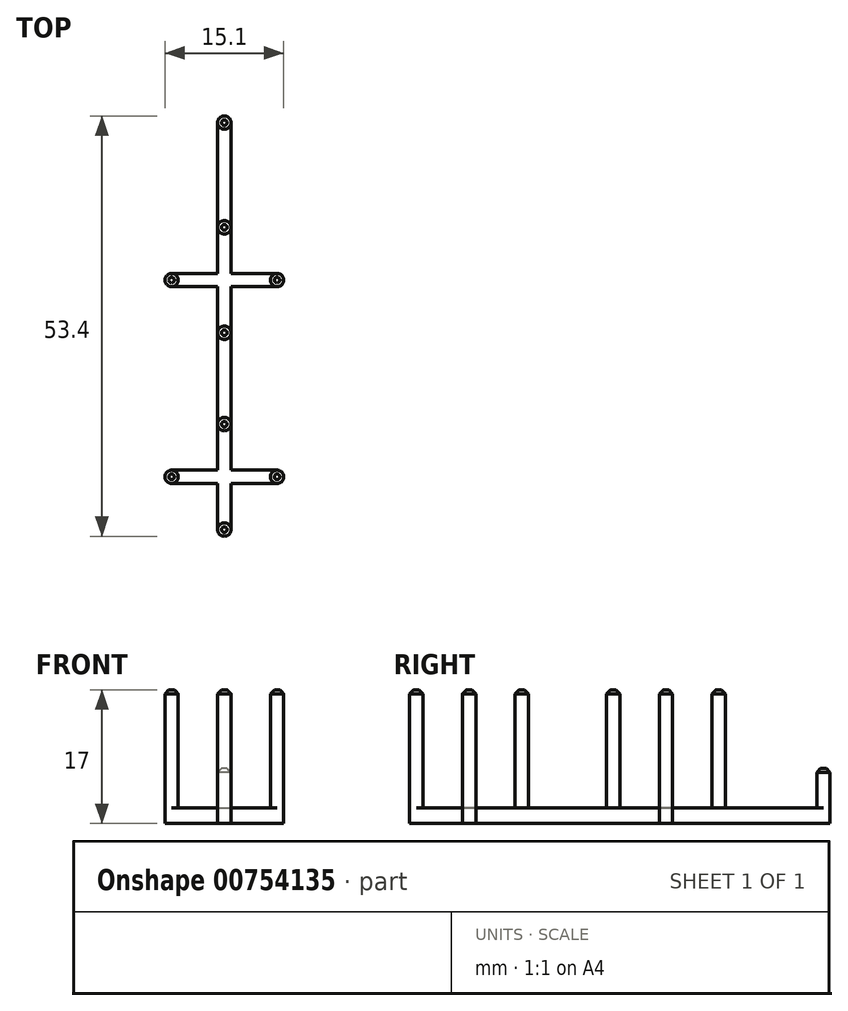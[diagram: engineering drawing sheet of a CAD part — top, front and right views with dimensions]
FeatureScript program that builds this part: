
annotation { "Feature Type Name" : "Feature", "Feature Type Description" : "" }
export const myFeature = defineFeature(function(context is Context, id is Id, definition is map)
    precondition{}
    {
        {
            var Q0;
            Q0=qCreatedBy(makeId("Top.planeOp"),FACE);
            var sketch = newSketch(context, id + "F0", { "sketchPlane" : qUnion([Q0])});
            skLineSegment(sketch, "E0", {"start": v(-6.7, 0) * mm, "end": v(6.7, 0) * mm});
            skLineSegment(sketch, "E1", {"start": v(0, -6.7) * mm, "end": v(0, 6.7) * mm});
            skCircle(sketch, "E2", {"center": v(-6.7, 0) * mm, "radius": 0.85 * mm});
            skCircle(sketch, "E3", {"center": v(0, -6.7) * mm, "radius": 0.85 * mm});
            skCircle(sketch, "E4", {"center": v(6.7, 0) * mm, "radius": 0.85 * mm});
            skCircle(sketch, "E5", {"center": v(0, 6.7) * mm, "radius": 0.85 * mm});
            skLineSegment(sketch, "E6.top", {"start": v(-0.85, 45) * mm, "end": v(0.85, 45) * mm});
            skCircle(sketch, "E7", {"center": v(0, 18.3) * mm, "radius": 0.85 * mm});
            skCircle(sketch, "E8", {"center": v(0, 31.7) * mm, "radius": 0.85 * mm});
            skLineSegment(sketch, "E9", {"start": v(0, 18.3) * mm, "end": v(0, 31.7) * mm});
            skPoint(sketch, "E10", {"position": v(0, 25) * mm});
            skLineSegment(sketch, "E11", {"start": v(-6.7, 25) * mm, "end": v(6.7, 25) * mm});
            skCircle(sketch, "E12", {"center": v(-6.7, 25) * mm, "radius": 0.85 * mm});
            skCircle(sketch, "E13", {"center": v(6.7, 25) * mm, "radius": 0.85 * mm});
            skLineSegment(sketch, "E14.bottom", {"start": v(-7.55, 24.15) * mm, "end": v(7.55, 24.15) * mm});
            skLineSegment(sketch, "E14.top", {"start": v(-7.55, 25.85) * mm, "end": v(7.55, 25.85) * mm});
            skLineSegment(sketch, "E14.left", {"start": v(-7.55, 24.15) * mm, "end": v(-7.55, 25.85) * mm});
            skLineSegment(sketch, "E14.right", {"start": v(7.55, 24.15) * mm, "end": v(7.55, 25.85) * mm});
            skCircle(sketch, "E15", {"center": v(0, 45) * mm, "radius": 0.85 * mm});
            skLineSegment(sketch, "E16", {"start": v(-6.7, -0.85) * mm, "end": v(6.7, -0.85) * mm});
            skLineSegment(sketch, "E17", {"start": v(-6.7, 0.85) * mm, "end": v(6.7, 0.85) * mm});
            skLineSegment(sketch, "E18", {"start": v(0.85, -6.7) * mm, "end": v(0.85, 45) * mm});
            skLineSegment(sketch, "E19", {"start": v(-0.85, -6.7) * mm, "end": v(-0.85, 45) * mm});
            skSolve(sketch);
        }
        {
            var Q0;
            {var subQ5=sQuery(id+"F0.wireOp",EDGE,"E6.top");Q0=makeQuery(id+"F0.imprint","IMPRINT",FACE,{"disambiguationData":[TD([[makeQuery(id+"F0.imprint","IMPRINT",EDGE,{"derivedFrom":subQ5}),-1.0]])]});}
            var Q1;
            {var subQ0=sQuery(id+"F0.wireOp",EDGE,"E5");var subQ1=makeQuery(id+"F0.imprint","INTERSECT",VERTEX,{"derivedFrom":[subQ0,sQuery(id+"F0.wireOp",EDGE,"E6.left")]});Q1=makeQuery(id+"F0.imprint","IMPRINT",FACE,{"disambiguationData":[TD([[makeQuery(id+"F0.imprint","IMPRINT",EDGE,{"disambiguationData":[TD([[subQ1,1.0]])],"derivedFrom":subQ0}),1.0]])]});}
            var Q2;
            {var subQ0=sQuery(id+"F0.wireOp",EDGE,"E5");var subQ1=sQuery(id+"F0.wireOp",EDGE,"E1");var subQ2=makeQuery(id+"F0.imprint","INTERSECT",VERTEX,{"derivedFrom":[subQ1,subQ0]});Q2=makeQuery(id+"F0.imprint","IMPRINT",FACE,{"disambiguationData":[TD([[makeQuery(id+"F0.imprint","IMPRINT",EDGE,{"disambiguationData":[TD([[subQ2,1.0]])],"derivedFrom":subQ1}),-1.0]])]});}
            var Q3;
            {var subQ0=sQuery(id+"F0.wireOp",EDGE,"E5");var subQ1=sQuery(id+"F0.wireOp",EDGE,"E1");var subQ2=makeQuery(id+"F0.imprint","INTERSECT",VERTEX,{"derivedFrom":[subQ1,subQ0]});Q3=makeQuery(id+"F0.imprint","IMPRINT",FACE,{"disambiguationData":[TD([[makeQuery(id+"F0.imprint","IMPRINT",EDGE,{"disambiguationData":[TD([[subQ2,1.0]])],"derivedFrom":subQ1}),1.0]])]});}
            var Q4;
            {var subQ0=sQuery(id+"F0.wireOp",EDGE,"E6.left");var subQ1=sQuery(id+"F0.wireOp",EDGE,"E0");var subQ2=makeQuery(id+"F0.imprint","INTERSECT",VERTEX,{"derivedFrom":[subQ1,subQ0]});Q4=makeQuery(id+"F0.imprint","IMPRINT",FACE,{"disambiguationData":[TD([[makeQuery(id+"F0.imprint","IMPRINT",EDGE,{"disambiguationData":[TD([[subQ2,-1.0]])],"derivedFrom":subQ1}),1.0]])]});}
            var Q5;
            {var subQ0=sQuery(id+"F0.wireOp",EDGE,"E2");var subQ1=sQuery(id+"F0.wireOp",EDGE,"E0");var subQ2=makeQuery(id+"F0.imprint","INTERSECT",VERTEX,{"derivedFrom":[subQ1,subQ0]});Q5=makeQuery(id+"F0.imprint","IMPRINT",FACE,{"disambiguationData":[TD([[makeQuery(id+"F0.imprint","IMPRINT",EDGE,{"disambiguationData":[TD([[subQ2,-1.0]])],"derivedFrom":subQ1}),-1.0]])]});}
            var Q6;
            {var subQ0=sQuery(id+"F0.wireOp",EDGE,"E2");var subQ1=makeQuery(id+"F0.imprint","INTERSECT",VERTEX,{"derivedFrom":[sQuery(id+"F0.wireOp",EDGE,"E0"),subQ0]});Q6=makeQuery(id+"F0.imprint","IMPRINT",FACE,{"disambiguationData":[TD([[makeQuery(id+"F0.imprint","IMPRINT",EDGE,{"disambiguationData":[TD([[subQ1,-1.0]])],"derivedFrom":subQ0}),1.0]])]});}
            var Q7;
            {var subQ0=sQuery(id+"F0.wireOp",EDGE,"E1");var subQ1=sQuery(id+"F0.wireOp",EDGE,"E0");var subQ2=makeQuery(id+"F0.imprint","INTERSECT",VERTEX,{"derivedFrom":[subQ1,subQ0]});Q7=makeQuery(id+"F0.imprint","IMPRINT",FACE,{"disambiguationData":[TD([[makeQuery(id+"F0.imprint","IMPRINT",EDGE,{"disambiguationData":[TD([[subQ2,-1.0]])],"derivedFrom":subQ1}),1.0]])]});}
            var Q8;
            {var subQ0=sQuery(id+"F0.wireOp",EDGE,"E1");var subQ1=sQuery(id+"F0.wireOp",EDGE,"E0");var subQ2=makeQuery(id+"F0.imprint","INTERSECT",VERTEX,{"derivedFrom":[subQ1,subQ0]});Q8=makeQuery(id+"F0.imprint","IMPRINT",FACE,{"disambiguationData":[TD([[makeQuery(id+"F0.imprint","IMPRINT",EDGE,{"disambiguationData":[TD([[subQ2,-1.0]])],"derivedFrom":subQ1}),-1.0]])]});}
            var Q9;
            {var subQ0=sQuery(id+"F0.wireOp",EDGE,"E6.left");var subQ1=sQuery(id+"F0.wireOp",EDGE,"E0");var subQ2=makeQuery(id+"F0.imprint","INTERSECT",VERTEX,{"derivedFrom":[subQ1,subQ0]});Q9=makeQuery(id+"F0.imprint","IMPRINT",FACE,{"disambiguationData":[TD([[makeQuery(id+"F0.imprint","IMPRINT",EDGE,{"disambiguationData":[TD([[subQ2,-1.0]])],"derivedFrom":subQ1}),-1.0]])]});}
            var Q10;
            {var subQ0=sQuery(id+"F0.wireOp",EDGE,"E2");var subQ1=sQuery(id+"F0.wireOp",EDGE,"E0");var subQ2=makeQuery(id+"F0.imprint","INTERSECT",VERTEX,{"derivedFrom":[subQ1,subQ0]});Q10=makeQuery(id+"F0.imprint","IMPRINT",FACE,{"disambiguationData":[TD([[makeQuery(id+"F0.imprint","IMPRINT",EDGE,{"disambiguationData":[TD([[subQ2,-1.0]])],"derivedFrom":subQ1}),1.0]])]});}
            var Q11;
            {var subQ0=sQuery(id+"F0.wireOp",EDGE,"E4");var subQ1=sQuery(id+"F0.wireOp",EDGE,"E0");var subQ2=makeQuery(id+"F0.imprint","INTERSECT",VERTEX,{"derivedFrom":[subQ1,subQ0]});Q11=makeQuery(id+"F0.imprint","IMPRINT",FACE,{"disambiguationData":[TD([[makeQuery(id+"F0.imprint","IMPRINT",EDGE,{"disambiguationData":[TD([[subQ2,1.0]])],"derivedFrom":subQ1}),1.0]])]});}
            var Q12;
            {var subQ0=sQuery(id+"F0.wireOp",EDGE,"E4");var subQ1=makeQuery(id+"F0.imprint","INTERSECT",VERTEX,{"derivedFrom":[subQ0,sQuery(id+"F0.wireOp",EDGE,"UeLpGbLd-B8RJ-5YED-L5t8-W8zW61iBtvWg.bottom")]});Q12=makeQuery(id+"F0.imprint","IMPRINT",FACE,{"disambiguationData":[TD([[makeQuery(id+"F0.imprint","IMPRINT",EDGE,{"disambiguationData":[TD([[subQ1,1.0]])],"derivedFrom":subQ0}),1.0]])]});}
            var Q13;
            {var subQ0=sQuery(id+"F0.wireOp",EDGE,"E4");var subQ1=sQuery(id+"F0.wireOp",EDGE,"E0");var subQ2=makeQuery(id+"F0.imprint","INTERSECT",VERTEX,{"derivedFrom":[subQ1,subQ0]});Q13=makeQuery(id+"F0.imprint","IMPRINT",FACE,{"disambiguationData":[TD([[makeQuery(id+"F0.imprint","IMPRINT",EDGE,{"disambiguationData":[TD([[subQ2,1.0]])],"derivedFrom":subQ1}),-1.0]])]});}
            var Q14;
            {var subQ0=sQuery(id+"F0.wireOp",EDGE,"E3");var subQ1=sQuery(id+"F0.wireOp",EDGE,"E1");var subQ2=makeQuery(id+"F0.imprint","INTERSECT",VERTEX,{"derivedFrom":[subQ1,subQ0]});Q14=makeQuery(id+"F0.imprint","IMPRINT",FACE,{"disambiguationData":[TD([[makeQuery(id+"F0.imprint","IMPRINT",EDGE,{"disambiguationData":[TD([[subQ2,-1.0]])],"derivedFrom":subQ1}),-1.0]])]});}
            var Q15;
            {var subQ0=sQuery(id+"F0.wireOp",EDGE,"E3");var subQ1=sQuery(id+"F0.wireOp",EDGE,"E1");var subQ2=makeQuery(id+"F0.imprint","INTERSECT",VERTEX,{"derivedFrom":[subQ1,subQ0]});Q15=makeQuery(id+"F0.imprint","IMPRINT",FACE,{"disambiguationData":[TD([[makeQuery(id+"F0.imprint","IMPRINT",EDGE,{"disambiguationData":[TD([[subQ2,-1.0]])],"derivedFrom":subQ1}),1.0]])]});}
            var Q16;
            {var subQ0=sQuery(id+"F0.wireOp",EDGE,"E3");var subQ1=makeQuery(id+"F0.imprint","INTERSECT",VERTEX,{"derivedFrom":[sQuery(id+"F0.wireOp",EDGE,"E1"),subQ0]});Q16=makeQuery(id+"F0.imprint","IMPRINT",FACE,{"disambiguationData":[TD([[makeQuery(id+"F0.imprint","IMPRINT",EDGE,{"disambiguationData":[TD([[subQ1,1.0]])],"derivedFrom":subQ0}),1.0]])]});}
            var Q17;
            {var subQ0=sQuery(id+"F0.wireOp",EDGE,"E6.left");var subQ1=sQuery(id+"F0.wireOp",EDGE,"E5");var subQ2=makeQuery(id+"F0.imprint","INTERSECT",VERTEX,{"derivedFrom":[subQ1,subQ0]});Q17=makeQuery(id+"F0.imprint","IMPRINT",FACE,{"disambiguationData":[TD([[makeQuery(id+"F0.imprint","IMPRINT",EDGE,{"disambiguationData":[TD([[subQ2,1.0]])],"derivedFrom":subQ1}),-1.0]])]});}
            var Q18;
            {var subQ0=sQuery(id+"F0.wireOp",EDGE,"E7");var subQ1=makeQuery(id+"F0.imprint","INTERSECT",VERTEX,{"derivedFrom":[sQuery(id+"F0.wireOp",EDGE,"E6.right"),subQ0]});Q18=makeQuery(id+"F0.imprint","IMPRINT",FACE,{"disambiguationData":[TD([[makeQuery(id+"F0.imprint","IMPRINT",EDGE,{"disambiguationData":[TD([[subQ1,-1.0]])],"derivedFrom":subQ0}),1.0]])]});}
            var Q19;
            {var subQ0=sQuery(id+"F0.wireOp",EDGE,"E7");var subQ1=sQuery(id+"F0.wireOp",EDGE,"E6.right");var subQ2=makeQuery(id+"F0.imprint","INTERSECT",VERTEX,{"derivedFrom":[subQ1,subQ0]});Q19=makeQuery(id+"F0.imprint","IMPRINT",FACE,{"disambiguationData":[TD([[makeQuery(id+"F0.imprint","IMPRINT",EDGE,{"disambiguationData":[TD([[subQ2,-1.0]])],"derivedFrom":subQ1}),1.0]])]});}
            var Q20;
            {var subQ0=sQuery(id+"F0.wireOp",EDGE,"E14.bottom");var subQ1=sQuery(id+"F0.wireOp",EDGE,"E6.right");var subQ2=makeQuery(id+"F0.imprint","INTERSECT",VERTEX,{"derivedFrom":[subQ1,subQ0]});Q20=makeQuery(id+"F0.imprint","IMPRINT",FACE,{"disambiguationData":[TD([[makeQuery(id+"F0.imprint","IMPRINT",EDGE,{"disambiguationData":[TD([[subQ2,-1.0]])],"derivedFrom":subQ1}),1.0]])]});}
            var Q21;
            {var subQ0=sQuery(id+"F0.wireOp",EDGE,"E14.top");var subQ1=sQuery(id+"F0.wireOp",EDGE,"E6.right");var subQ2=makeQuery(id+"F0.imprint","INTERSECT",VERTEX,{"derivedFrom":[subQ1,subQ0]});Q21=makeQuery(id+"F0.imprint","IMPRINT",FACE,{"disambiguationData":[TD([[makeQuery(id+"F0.imprint","IMPRINT",EDGE,{"disambiguationData":[TD([[subQ2,1.0]])],"derivedFrom":subQ1}),1.0]])]});}
            var Q22;
            {var subQ0=sQuery(id+"F0.wireOp",EDGE,"E14.top");var subQ1=sQuery(id+"F0.wireOp",EDGE,"E6.right");var subQ2=makeQuery(id+"F0.imprint","INTERSECT",VERTEX,{"derivedFrom":[subQ1,subQ0]});Q22=makeQuery(id+"F0.imprint","IMPRINT",FACE,{"disambiguationData":[TD([[makeQuery(id+"F0.imprint","IMPRINT",EDGE,{"disambiguationData":[TD([[subQ2,-1.0]])],"derivedFrom":subQ1}),1.0]])]});}
            var Q23;
            {var subQ0=sQuery(id+"F0.wireOp",EDGE,"E14.top");var subQ1=sQuery(id+"F0.wireOp",EDGE,"E6.right");var subQ2=makeQuery(id+"F0.imprint","INTERSECT",VERTEX,{"derivedFrom":[subQ1,subQ0]});Q23=makeQuery(id+"F0.imprint","IMPRINT",FACE,{"disambiguationData":[TD([[makeQuery(id+"F0.imprint","IMPRINT",EDGE,{"disambiguationData":[TD([[subQ2,1.0]])],"derivedFrom":subQ1}),-1.0]])]});}
            var Q24;
            {var subQ0=sQuery(id+"F0.wireOp",EDGE,"E14.bottom");var subQ1=sQuery(id+"F0.wireOp",EDGE,"E6.right");var subQ2=makeQuery(id+"F0.imprint","INTERSECT",VERTEX,{"derivedFrom":[subQ1,subQ0]});Q24=makeQuery(id+"F0.imprint","IMPRINT",FACE,{"disambiguationData":[TD([[makeQuery(id+"F0.imprint","IMPRINT",EDGE,{"disambiguationData":[TD([[subQ2,-1.0]])],"derivedFrom":subQ1}),-1.0]])]});}
            var Q25;
            {var subQ0=sQuery(id+"F0.wireOp",EDGE,"E13");var subQ1=makeQuery(id+"F0.imprint","INTERSECT",VERTEX,{"derivedFrom":[subQ0,sQuery(id+"F0.wireOp",EDGE,"E14.top")]});Q25=makeQuery(id+"F0.imprint","IMPRINT",FACE,{"disambiguationData":[TD([[makeQuery(id+"F0.imprint","IMPRINT",EDGE,{"disambiguationData":[TD([[subQ1,1.0]])],"derivedFrom":subQ0}),1.0]])]});}
            var Q26;
            {var subQ0=sQuery(id+"F0.wireOp",EDGE,"E7");var subQ1=sQuery(id+"F0.wireOp",EDGE,"E6.left");var subQ2=makeQuery(id+"F0.imprint","INTERSECT",VERTEX,{"derivedFrom":[subQ1,subQ0]});Q26=makeQuery(id+"F0.imprint","IMPRINT",FACE,{"disambiguationData":[TD([[makeQuery(id+"F0.imprint","IMPRINT",EDGE,{"disambiguationData":[TD([[subQ2,-1.0]])],"derivedFrom":subQ1}),-1.0]])]});}
            var Q27;
            {var subQ0=sQuery(id+"F0.wireOp",EDGE,"E14.bottom");var subQ1=sQuery(id+"F0.wireOp",EDGE,"E6.left");var subQ2=makeQuery(id+"F0.imprint","INTERSECT",VERTEX,{"derivedFrom":[subQ1,subQ0]});Q27=makeQuery(id+"F0.imprint","IMPRINT",FACE,{"disambiguationData":[TD([[makeQuery(id+"F0.imprint","IMPRINT",EDGE,{"disambiguationData":[TD([[subQ2,-1.0]])],"derivedFrom":subQ1}),-1.0]])]});}
            var Q28;
            {var subQ0=sQuery(id+"F0.wireOp",EDGE,"E14.top");var subQ1=sQuery(id+"F0.wireOp",EDGE,"E6.left");var subQ2=makeQuery(id+"F0.imprint","INTERSECT",VERTEX,{"derivedFrom":[subQ1,subQ0]});Q28=makeQuery(id+"F0.imprint","IMPRINT",FACE,{"disambiguationData":[TD([[makeQuery(id+"F0.imprint","IMPRINT",EDGE,{"disambiguationData":[TD([[subQ2,1.0]])],"derivedFrom":subQ1}),-1.0]])]});}
            var Q29;
            {var subQ0=sQuery(id+"F0.wireOp",EDGE,"E14.top");var subQ1=sQuery(id+"F0.wireOp",EDGE,"E6.left");var subQ2=makeQuery(id+"F0.imprint","INTERSECT",VERTEX,{"derivedFrom":[subQ1,subQ0]});Q29=makeQuery(id+"F0.imprint","IMPRINT",FACE,{"disambiguationData":[TD([[makeQuery(id+"F0.imprint","IMPRINT",EDGE,{"disambiguationData":[TD([[subQ2,1.0]])],"derivedFrom":subQ1}),1.0]])]});}
            var Q30;
            {var subQ0=sQuery(id+"F0.wireOp",EDGE,"E14.bottom");var subQ1=sQuery(id+"F0.wireOp",EDGE,"E6.left");var subQ2=makeQuery(id+"F0.imprint","INTERSECT",VERTEX,{"derivedFrom":[subQ1,subQ0]});Q30=makeQuery(id+"F0.imprint","IMPRINT",FACE,{"disambiguationData":[TD([[makeQuery(id+"F0.imprint","IMPRINT",EDGE,{"disambiguationData":[TD([[subQ2,-1.0]])],"derivedFrom":subQ1}),1.0]])]});}
            var Q31;
            {var subQ0=sQuery(id+"F0.wireOp",EDGE,"E12");var subQ1=makeQuery(id+"F0.imprint","INTERSECT",VERTEX,{"derivedFrom":[sQuery(id+"F0.wireOp",EDGE,"E11"),subQ0]});Q31=makeQuery(id+"F0.imprint","IMPRINT",FACE,{"disambiguationData":[TD([[makeQuery(id+"F0.imprint","IMPRINT",EDGE,{"disambiguationData":[TD([[subQ1,-1.0]])],"derivedFrom":subQ0}),1.0]])]});}
            var Q32;
            {var subQ0=sQuery(id+"F0.wireOp",EDGE,"E14.top");var subQ1=sQuery(id+"F0.wireOp",EDGE,"E6.left");var subQ2=makeQuery(id+"F0.imprint","INTERSECT",VERTEX,{"derivedFrom":[subQ1,subQ0]});Q32=makeQuery(id+"F0.imprint","IMPRINT",FACE,{"disambiguationData":[TD([[makeQuery(id+"F0.imprint","IMPRINT",EDGE,{"disambiguationData":[TD([[subQ2,-1.0]])],"derivedFrom":subQ1}),-1.0]])]});}
            var Q33;
            {var subQ0=sQuery(id+"F0.wireOp",EDGE,"E8");var subQ1=makeQuery(id+"F0.imprint","INTERSECT",VERTEX,{"derivedFrom":[sQuery(id+"F0.wireOp",EDGE,"E6.left"),subQ0]});Q33=makeQuery(id+"F0.imprint","IMPRINT",FACE,{"disambiguationData":[TD([[makeQuery(id+"F0.imprint","IMPRINT",EDGE,{"disambiguationData":[TD([[subQ1,1.0]])],"derivedFrom":subQ0}),1.0]])]});}
            var Q34;
            {var subQ1=sQuery(id+"F0.wireOp",EDGE,"E6.left");var subQ4=sQuery(id+"F0.wireOp",EDGE,"E8");var subQ5=makeQuery(id+"F0.imprint","INTERSECT",VERTEX,{"derivedFrom":[subQ1,subQ4]});Q34=makeQuery(id+"F0.imprint","IMPRINT",FACE,{"disambiguationData":[TD([[makeQuery(id+"F0.imprint","IMPRINT",EDGE,{"disambiguationData":[TD([[subQ5,1.0]])],"derivedFrom":subQ4}),-1.0]])]});}
            var Q35;
            {var subQ0=sQuery(id+"F0.wireOp",EDGE,"E9");var subQ1=sQuery(id+"F0.wireOp",EDGE,"E7");var subQ2=makeQuery(id+"F0.imprint","INTERSECT",VERTEX,{"derivedFrom":[subQ1,subQ0]});Q35=makeQuery(id+"F0.imprint","IMPRINT",FACE,{"disambiguationData":[TD([[makeQuery(id+"F0.imprint","IMPRINT",EDGE,{"disambiguationData":[TD([[subQ2,1.0]])],"derivedFrom":subQ1}),-1.0]])]});}
            var Q36;
            {var subQ0=sQuery(id+"F0.wireOp",EDGE,"E9");var subQ1=sQuery(id+"F0.wireOp",EDGE,"E7");var subQ2=makeQuery(id+"F0.imprint","INTERSECT",VERTEX,{"derivedFrom":[subQ1,subQ0]});Q36=makeQuery(id+"F0.imprint","IMPRINT",FACE,{"disambiguationData":[TD([[makeQuery(id+"F0.imprint","IMPRINT",EDGE,{"disambiguationData":[TD([[subQ2,-1.0]])],"derivedFrom":subQ1}),-1.0]])]});}
            var Q37;
            {var subQ0=sQuery(id+"F0.wireOp",EDGE,"E14.bottom");var subQ1=sQuery(id+"F0.wireOp",EDGE,"E9");var subQ2=makeQuery(id+"F0.imprint","INTERSECT",VERTEX,{"derivedFrom":[subQ1,subQ0]});Q37=makeQuery(id+"F0.imprint","IMPRINT",FACE,{"disambiguationData":[TD([[makeQuery(id+"F0.imprint","IMPRINT",EDGE,{"disambiguationData":[TD([[subQ2,-1.0]])],"derivedFrom":subQ1}),-1.0]])]});}
            var Q38;
            {var subQ0=sQuery(id+"F0.wireOp",EDGE,"E14.bottom");var subQ1=sQuery(id+"F0.wireOp",EDGE,"E9");var subQ2=makeQuery(id+"F0.imprint","INTERSECT",VERTEX,{"derivedFrom":[subQ1,subQ0]});Q38=makeQuery(id+"F0.imprint","IMPRINT",FACE,{"disambiguationData":[TD([[makeQuery(id+"F0.imprint","IMPRINT",EDGE,{"disambiguationData":[TD([[subQ2,-1.0]])],"derivedFrom":subQ1}),1.0]])]});}
            var Q39;
            {var subQ0=sQuery(id+"F0.wireOp",EDGE,"E11");var subQ1=sQuery(id+"F0.wireOp",EDGE,"E9");var subQ2=makeQuery(id+"F0.imprint","INTERSECT",VERTEX,{"derivedFrom":[subQ1,subQ0]});Q39=makeQuery(id+"F0.imprint","IMPRINT",FACE,{"disambiguationData":[TD([[makeQuery(id+"F0.imprint","IMPRINT",EDGE,{"disambiguationData":[TD([[subQ2,-1.0]])],"derivedFrom":subQ1}),1.0]])]});}
            var Q40;
            {var subQ0=sQuery(id+"F0.wireOp",EDGE,"E11");var subQ1=sQuery(id+"F0.wireOp",EDGE,"E9");var subQ2=makeQuery(id+"F0.imprint","INTERSECT",VERTEX,{"derivedFrom":[subQ1,subQ0]});Q40=makeQuery(id+"F0.imprint","IMPRINT",FACE,{"disambiguationData":[TD([[makeQuery(id+"F0.imprint","IMPRINT",EDGE,{"disambiguationData":[TD([[subQ2,-1.0]])],"derivedFrom":subQ1}),-1.0]])]});}
            var Q41;
            {var subQ0=sQuery(id+"F0.wireOp",EDGE,"E13");var subQ1=sQuery(id+"F0.wireOp",EDGE,"E11");var subQ2=makeQuery(id+"F0.imprint","INTERSECT",VERTEX,{"derivedFrom":[subQ1,subQ0]});Q41=makeQuery(id+"F0.imprint","IMPRINT",FACE,{"disambiguationData":[TD([[makeQuery(id+"F0.imprint","IMPRINT",EDGE,{"disambiguationData":[TD([[subQ2,1.0]])],"derivedFrom":subQ1}),1.0]])]});}
            var Q42;
            {var subQ0=sQuery(id+"F0.wireOp",EDGE,"E13");var subQ1=sQuery(id+"F0.wireOp",EDGE,"E11");var subQ2=makeQuery(id+"F0.imprint","INTERSECT",VERTEX,{"derivedFrom":[subQ1,subQ0]});Q42=makeQuery(id+"F0.imprint","IMPRINT",FACE,{"disambiguationData":[TD([[makeQuery(id+"F0.imprint","IMPRINT",EDGE,{"disambiguationData":[TD([[subQ2,1.0]])],"derivedFrom":subQ1}),-1.0]])]});}
            var Q43;
            {var subQ0=sQuery(id+"F0.wireOp",EDGE,"E12");var subQ1=sQuery(id+"F0.wireOp",EDGE,"E11");var subQ2=makeQuery(id+"F0.imprint","INTERSECT",VERTEX,{"derivedFrom":[subQ1,subQ0]});Q43=makeQuery(id+"F0.imprint","IMPRINT",FACE,{"disambiguationData":[TD([[makeQuery(id+"F0.imprint","IMPRINT",EDGE,{"disambiguationData":[TD([[subQ2,-1.0]])],"derivedFrom":subQ1}),-1.0]])]});}
            var Q44;
            {var subQ0=sQuery(id+"F0.wireOp",EDGE,"E12");var subQ1=sQuery(id+"F0.wireOp",EDGE,"E11");var subQ2=makeQuery(id+"F0.imprint","INTERSECT",VERTEX,{"derivedFrom":[subQ1,subQ0]});Q44=makeQuery(id+"F0.imprint","IMPRINT",FACE,{"disambiguationData":[TD([[makeQuery(id+"F0.imprint","IMPRINT",EDGE,{"disambiguationData":[TD([[subQ2,-1.0]])],"derivedFrom":subQ1}),1.0]])]});}
            var Q45;
            {var subQ0=sQuery(id+"F0.wireOp",EDGE,"E6.top");Q45=makeQuery(id+"F0.imprint","IMPRINT",FACE,{"disambiguationData":[TD([[makeQuery(id+"F0.imprint","IMPRINT",EDGE,{"derivedFrom":subQ0}),1.0]])]});}
            extrude(context, id + "F1", {"entities" : qUnion([Q0, Q1, Q2, Q3, Q4, Q5, Q6, Q7, Q8, Q9, Q10, Q11, Q12, Q13, Q14, Q15, Q16, Q17, Q18, Q19, Q20, Q21, Q22, Q23, Q24, Q25, Q26, Q27, Q28, Q29, Q30, Q31, Q32, Q33, Q34, Q35, Q36, Q37, Q38, Q39, Q40, Q41, Q42, Q43, Q44, Q45]), "oppositeDirection" : true, "depth" : 2 * mm, "offsetDistance" : 25 * mm});
        }
        {
            var Q0;
            {var subQ0=sQuery(id+"F0.wireOp",EDGE,"E2");var subQ1=makeQuery(id+"F0.imprint","INTERSECT",VERTEX,{"derivedFrom":[sQuery(id+"F0.wireOp",EDGE,"E0"),subQ0]});Q0=makeQuery(id+"F0.imprint","IMPRINT",FACE,{"disambiguationData":[TD([[makeQuery(id+"F0.imprint","IMPRINT",EDGE,{"disambiguationData":[TD([[subQ1,-1.0]])],"derivedFrom":subQ0}),1.0]])]});}
            var Q1;
            {var subQ0=sQuery(id+"F0.wireOp",EDGE,"E5");var subQ1=makeQuery(id+"F0.imprint","INTERSECT",VERTEX,{"derivedFrom":[subQ0,sQuery(id+"F0.wireOp",EDGE,"E6.left")]});Q1=makeQuery(id+"F0.imprint","IMPRINT",FACE,{"disambiguationData":[TD([[makeQuery(id+"F0.imprint","IMPRINT",EDGE,{"disambiguationData":[TD([[subQ1,1.0]])],"derivedFrom":subQ0}),1.0]])]});}
            var Q2;
            {var subQ0=sQuery(id+"F0.wireOp",EDGE,"E4");var subQ1=makeQuery(id+"F0.imprint","INTERSECT",VERTEX,{"derivedFrom":[subQ0,sQuery(id+"F0.wireOp",EDGE,"UeLpGbLd-B8RJ-5YED-L5t8-W8zW61iBtvWg.bottom")]});Q2=makeQuery(id+"F0.imprint","IMPRINT",FACE,{"disambiguationData":[TD([[makeQuery(id+"F0.imprint","IMPRINT",EDGE,{"disambiguationData":[TD([[subQ1,1.0]])],"derivedFrom":subQ0}),1.0]])]});}
            var Q3;
            {var subQ0=sQuery(id+"F0.wireOp",EDGE,"E3");var subQ1=makeQuery(id+"F0.imprint","INTERSECT",VERTEX,{"derivedFrom":[sQuery(id+"F0.wireOp",EDGE,"E1"),subQ0]});Q3=makeQuery(id+"F0.imprint","IMPRINT",FACE,{"disambiguationData":[TD([[makeQuery(id+"F0.imprint","IMPRINT",EDGE,{"disambiguationData":[TD([[subQ1,1.0]])],"derivedFrom":subQ0}),1.0]])]});}
            var Q4;
            {var subQ0=sQuery(id+"F0.wireOp",EDGE,"E7");var subQ1=makeQuery(id+"F0.imprint","INTERSECT",VERTEX,{"derivedFrom":[sQuery(id+"F0.wireOp",EDGE,"E6.right"),subQ0]});Q4=makeQuery(id+"F0.imprint","IMPRINT",FACE,{"disambiguationData":[TD([[makeQuery(id+"F0.imprint","IMPRINT",EDGE,{"disambiguationData":[TD([[subQ1,-1.0]])],"derivedFrom":subQ0}),1.0]])]});}
            var Q5;
            {var subQ0=sQuery(id+"F0.wireOp",EDGE,"E12");var subQ1=makeQuery(id+"F0.imprint","INTERSECT",VERTEX,{"derivedFrom":[sQuery(id+"F0.wireOp",EDGE,"E11"),subQ0]});Q5=makeQuery(id+"F0.imprint","IMPRINT",FACE,{"disambiguationData":[TD([[makeQuery(id+"F0.imprint","IMPRINT",EDGE,{"disambiguationData":[TD([[subQ1,-1.0]])],"derivedFrom":subQ0}),1.0]])]});}
            var Q6;
            {var subQ0=sQuery(id+"F0.wireOp",EDGE,"E8");var subQ1=makeQuery(id+"F0.imprint","INTERSECT",VERTEX,{"derivedFrom":[sQuery(id+"F0.wireOp",EDGE,"E6.left"),subQ0]});Q6=makeQuery(id+"F0.imprint","IMPRINT",FACE,{"disambiguationData":[TD([[makeQuery(id+"F0.imprint","IMPRINT",EDGE,{"disambiguationData":[TD([[subQ1,1.0]])],"derivedFrom":subQ0}),1.0]])]});}
            var Q7;
            {var subQ0=sQuery(id+"F0.wireOp",EDGE,"E13");var subQ1=makeQuery(id+"F0.imprint","INTERSECT",VERTEX,{"derivedFrom":[subQ0,sQuery(id+"F0.wireOp",EDGE,"E14.top")]});Q7=makeQuery(id+"F0.imprint","IMPRINT",FACE,{"disambiguationData":[TD([[makeQuery(id+"F0.imprint","IMPRINT",EDGE,{"disambiguationData":[TD([[subQ1,1.0]])],"derivedFrom":subQ0}),1.0]])]});}
            extrude(context, id + "F2", {"entities" : qUnion([Q0, Q1, Q2, Q3, Q4, Q5, Q6, Q7]), "operationType" : NewBodyOperationType.ADD, "depth" : 15 * mm, "offsetDistance" : 25 * mm});
        }
        {
            var Q0;
            {var subQ0=sQuery(id+"F0.wireOp",EDGE,"E6.top");Q0=makeQuery(id+"F0.imprint","IMPRINT",FACE,{"disambiguationData":[TD([[makeQuery(id+"F0.imprint","IMPRINT",EDGE,{"derivedFrom":subQ0}),1.0]])]});}
            var Q1;
            {var subQ0=sQuery(id+"F0.wireOp",EDGE,"E6.top");Q1=makeQuery(id+"F0.imprint","IMPRINT",FACE,{"disambiguationData":[TD([[makeQuery(id+"F0.imprint","IMPRINT",EDGE,{"derivedFrom":subQ0}),-1.0]])]});}
            extrude(context, id + "F3", {"entities" : qUnion([Q0, Q1]), "operationType" : NewBodyOperationType.ADD, "depth" : 5 * mm, "offsetDistance" : 25 * mm});
        }
        {
            var Q0;
            Q0=makeQuery(id+"F2.opExtrude","CAP_EDGE",EDGE,{"disambiguationData":[OSD([sQuery(id+"F0.wireOp",EDGE,"E3")])],"isStart":false});
            var Q1;
            Q1=makeQuery(id+"F2.opExtrude","CAP_EDGE",EDGE,{"disambiguationData":[OSD([sQuery(id+"F0.wireOp",EDGE,"E2")])],"isStart":false});
            var Q2;
            Q2=makeQuery(id+"F2.opExtrude","CAP_EDGE",EDGE,{"disambiguationData":[OSD([sQuery(id+"F0.wireOp",EDGE,"E4")])],"isStart":false});
            var Q3;
            Q3=makeQuery(id+"F2.opExtrude","CAP_EDGE",EDGE,{"disambiguationData":[OSD([sQuery(id+"F0.wireOp",EDGE,"E5")])],"isStart":false});
            var Q4;
            Q4=makeQuery(id+"F2.opExtrude","CAP_EDGE",EDGE,{"disambiguationData":[OSD([sQuery(id+"F0.wireOp",EDGE,"E7")])],"isStart":false});
            var Q5;
            Q5=makeQuery(id+"F2.opExtrude","CAP_EDGE",EDGE,{"disambiguationData":[OSD([sQuery(id+"F0.wireOp",EDGE,"E13")])],"isStart":false});
            var Q6;
            Q6=makeQuery(id+"F2.opExtrude","CAP_EDGE",EDGE,{"disambiguationData":[OSD([sQuery(id+"F0.wireOp",EDGE,"E8")])],"isStart":false});
            var Q7;
            Q7=makeQuery(id+"F2.opExtrude","CAP_FACE",FACE,{"disambiguationData":[OSD([sQuery(id+"F0.wireOp",EDGE,"E12")])],"isStart":false});
            var Q8;
            Q8=makeQuery(id+"F2.opExtrude","CAP_EDGE",EDGE,{"disambiguationData":[OSD([sQuery(id+"F0.wireOp",EDGE,"E15")])],"isStart":false});
            var Q9;
            Q9=makeQuery(id+"F3.opExtrude","CAP_EDGE",EDGE,{"disambiguationData":[OSD([sQuery(id+"F0.wireOp",EDGE,"E15")])],"isStart":false});
            chamfer(context, id + "F4", {"entities" : qUnion([Q0, Q1, Q2, Q3, Q4, Q5, Q6, Q7, Q8, Q9]), "width" : 0.5 * mm, "tangentPropagation" : true});
        }
    });
